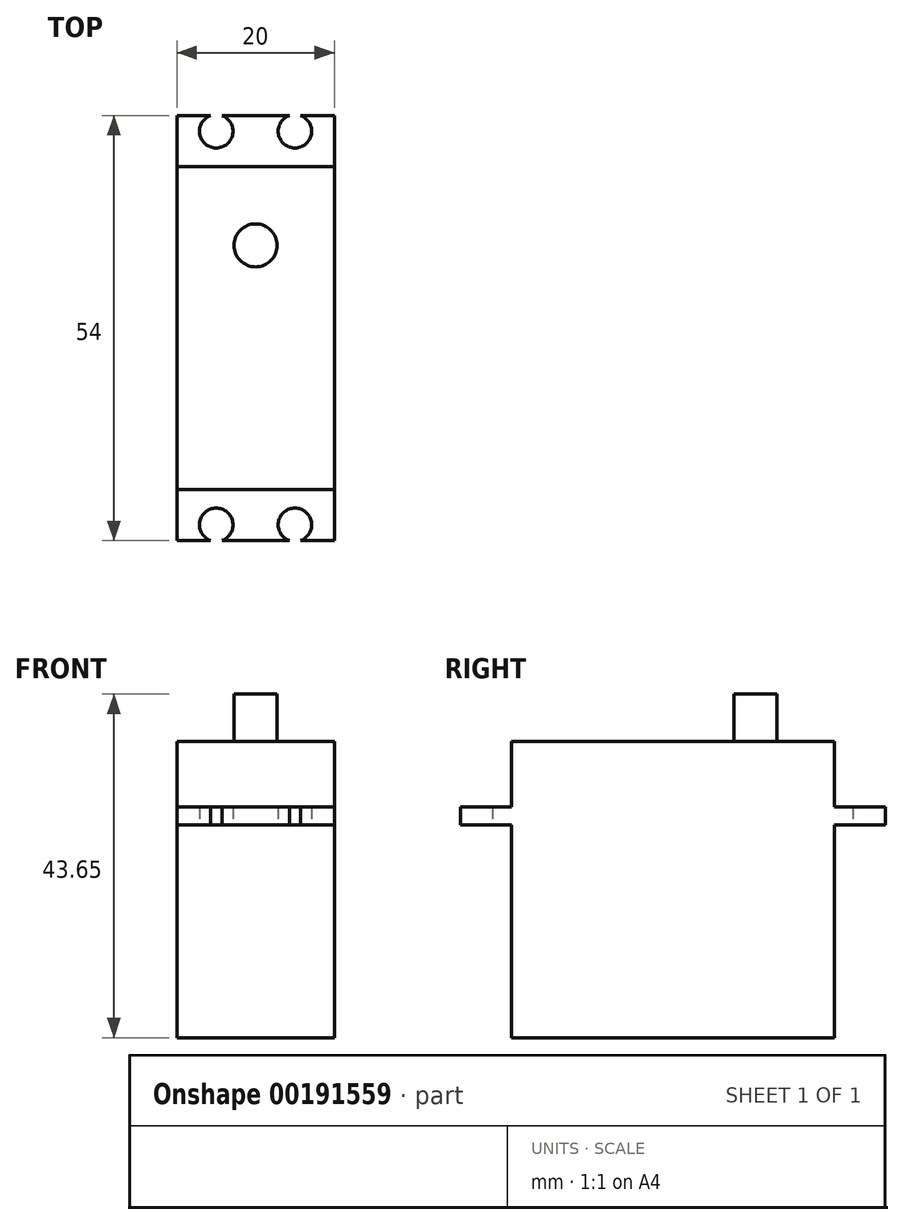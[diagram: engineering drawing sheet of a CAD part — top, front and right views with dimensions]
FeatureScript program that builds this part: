
annotation { "Feature Type Name" : "Feature", "Feature Type Description" : "" }
export const myFeature = defineFeature(function(context is Context, id is Id, definition is map)
    precondition{}
    {
        {
            var Q0;
            Q0=qCreatedBy(makeId("Top.planeOp"),FACE);
            var sketch = newSketch(context, id + "F0", { "sketchPlane" : qUnion([Q0])});
            skLineSegment(sketch, "E0.bottom", {"start": v(0, 0) * mm, "end": v(20, 0) * mm});
            skLineSegment(sketch, "E0.top", {"start": v(0, 41) * mm, "end": v(20, 41) * mm});
            skLineSegment(sketch, "E0.left", {"start": v(0, 0) * mm, "end": v(0, 41) * mm});
            skLineSegment(sketch, "E0.right", {"start": v(20, 0) * mm, "end": v(20, 41) * mm});
            skSolve(sketch);
        }
        {
            var Q0;
            Q0=makeQuery(id+"F0.imprint","IMPRINT",FACE,{"disambiguationData":[TD([[makeQuery(id+"F0.imprint","IMPRINT",EDGE,{"derivedFrom":sQuery(id+"F0.wireOp",EDGE,"E0.bottom")}),1.0]])]});
            extrude(context, id + "F1", {"entities" : qUnion([Q0]), "depth" : 27 * mm});
        }
        {
            var Q0;
            Q0=makeQuery(id+"F1.opExtrude","CAP_FACE",FACE,{"disambiguationData":[OSD([sQuery(id+"F0.wireOp",EDGE,"E0.bottom"),sQuery(id+"F0.wireOp",EDGE,"E0.top"),sQuery(id+"F0.wireOp",EDGE,"E0.left"),sQuery(id+"F0.wireOp",EDGE,"E0.right")])],"isStart":false});
            var sketch = newSketch(context, id + "F2", { "sketchPlane" : qUnion([Q0])});
            skLineSegment(sketch, "E1.bottom", {"start": v(20, 0) * mm, "end": v(0, 0) * mm});
            skLineSegment(sketch, "E1.top", {"start": v(20, -6.5) * mm, "end": v(0, -6.5) * mm});
            skLineSegment(sketch, "E1.left", {"start": v(20, 0) * mm, "end": v(20, -6.5) * mm});
            skLineSegment(sketch, "E1.right", {"start": v(0, 0) * mm, "end": v(0, -6.5) * mm});
            skLineSegment(sketch, "E2.bottom", {"start": v(20, 41) * mm, "end": v(0, 41) * mm});
            skLineSegment(sketch, "E2.top", {"start": v(20, 47.5) * mm, "end": v(0, 47.5) * mm});
            skLineSegment(sketch, "E2.left", {"start": v(20, 41) * mm, "end": v(20, 47.5) * mm});
            skLineSegment(sketch, "E2.right", {"start": v(0, 41) * mm, "end": v(0, 47.5) * mm});
            skCircle(sketch, "E3", {"center": v(15, -4.5) * mm, "radius": 2.12 * mm});
            skCircle(sketch, "E4", {"center": v(5, -4.5) * mm, "radius": 2.12 * mm});
            skLineSegment(sketch, "E5", {"start": v(0, 20.5) * mm, "end": v(8.39, 20.5) * mm, "construction": true});
            skCircle(sketch, "E6.MirrorC", {"center": v(15, 45.5) * mm, "radius": 2.12 * mm});
            skCircle(sketch, "E7.MirrorC", {"center": v(5, 45.5) * mm, "radius": 2.12 * mm});
            skSolve(sketch);
        }
        {
            var Q0;
            Q0=makeQuery(id+"F2.imprint","IMPRINT",FACE,{"disambiguationData":[TD([[makeQuery(id+"F2.imprint","IMPRINT",EDGE,{"derivedFrom":sQuery(id+"F2.wireOp",EDGE,"E1.bottom")}),1.0]])]});
            var Q1;
            Q1=makeQuery(id+"F2.imprint","IMPRINT",FACE,{"disambiguationData":[TD([[makeQuery(id+"F2.imprint","IMPRINT",EDGE,{"derivedFrom":sQuery(id+"F2.wireOp",EDGE,"E2.bottom")}),1.0]])]});
            var Q2;
            Q2=makeQuery(id+"F2.imprint","IMPRINT",FACE,{"disambiguationData":[TD([[makeQuery(id+"F2.imprint","IMPRINT",EDGE,{"derivedFrom":sQuery(id+"F2.wireOp",EDGE,"E1.bottom")}),-1.0]])]});
            extrude(context, id + "F3", {"entities" : qUnion([Q0, Q1, Q2]), "operationType" : NewBodyOperationType.ADD, "depth" : 2.3 * mm});
        }
        {
            var Q0;
            Q0=makeQuery(id+"F3.opExtrude","CAP_FACE",FACE,{"disambiguationData":[OSD([sQuery(id+"F0.wireOp",EDGE,"E0.left"),sQuery(id+"F0.wireOp",EDGE,"E0.right"),sQuery(id+"F2.wireOp",EDGE,"E1.top"),sQuery(id+"F2.wireOp",EDGE,"E1.left"),sQuery(id+"F2.wireOp",EDGE,"E1.right"),sQuery(id+"F2.wireOp",EDGE,"E2.top"),sQuery(id+"F2.wireOp",EDGE,"E2.left"),sQuery(id+"F2.wireOp",EDGE,"E2.right"),sQuery(id+"F2.wireOp",EDGE,"E3"),sQuery(id+"F2.wireOp",EDGE,"E4"),sQuery(id+"F2.wireOp",EDGE,"E6.MirrorC"),sQuery(id+"F2.wireOp",EDGE,"E7.MirrorC")])],"isStart":false});
            var sketch = newSketch(context, id + "F4", { "sketchPlane" : qUnion([Q0])});
            skLineSegment(sketch, "E8.0.0", {"start": v(0, 0) * mm, "end": v(0, 41) * mm});
            skLineSegment(sketch, "E8.0.1", {"start": v(0, 41) * mm, "end": v(20, 41) * mm});
            skLineSegment(sketch, "E8.0.2", {"start": v(20, 41) * mm, "end": v(20, 0) * mm});
            skLineSegment(sketch, "E8.0.3", {"start": v(20, 0) * mm, "end": v(0, 0) * mm});
            skSolve(sketch);
        }
        {
            var Q0;
            Q0=makeQuery(id+"F4.imprint","IMPRINT",FACE,{"disambiguationData":[TD([[makeQuery(id+"F4.imprint","IMPRINT",EDGE,{"derivedFrom":sQuery(id+"F4.wireOp",EDGE,"E8.0.0")}),-1.0]])]});
            extrude(context, id + "F5", {"entities" : qUnion([Q0]), "operationType" : NewBodyOperationType.ADD, "depth" : 8.35 * mm});
        }
        {
            var Q0;
            Q0=makeQuery(id+"F5.opExtrude","CAP_FACE",FACE,{"disambiguationData":[OSD([sQuery(id+"F4.wireOp",EDGE,"E8.0.0"),sQuery(id+"F4.wireOp",EDGE,"E8.0.1"),sQuery(id+"F4.wireOp",EDGE,"E8.0.2"),sQuery(id+"F4.wireOp",EDGE,"E8.0.3")])],"isStart":false});
            var sketch = newSketch(context, id + "F6", { "sketchPlane" : qUnion([Q0])});
            skCircle(sketch, "E9", {"center": v(10, 31) * mm, "radius": 2.73 * mm});
            skSolve(sketch);
        }
        {
            var Q0;
            Q0=makeQuery(id+"F6.imprint","IMPRINT",FACE,{"disambiguationData":[TD([[makeQuery(id+"F6.imprint","IMPRINT",EDGE,{"derivedFrom":sQuery(id+"F6.wireOp",EDGE,"E9")}),1.0]])]});
            extrude(context, id + "F7", {"entities" : qUnion([Q0]), "operationType" : NewBodyOperationType.ADD, "depth" : 6 * mm});
        }
        {
            var Q0;
            Q0=makeQuery(id+"F1.opExtrude","SWEPT_BODY",BODY,{"disambiguationData":[OSD([sQuery(id+"F0.wireOp",EDGE,"E0.bottom"),sQuery(id+"F0.wireOp",EDGE,"E0.top"),sQuery(id+"F0.wireOp",EDGE,"E0.left"),sQuery(id+"F0.wireOp",EDGE,"E0.right")])]});
            transform(context, id + "F8", {"entities" : qUnion([Q0]), "transformType" : TransformType.TRANSLATION_3D, "dx" : 0 * mm, "dy" : 0 * mm, "dz" : 0 * mm, "makeCopy" : true});
        }
    });
